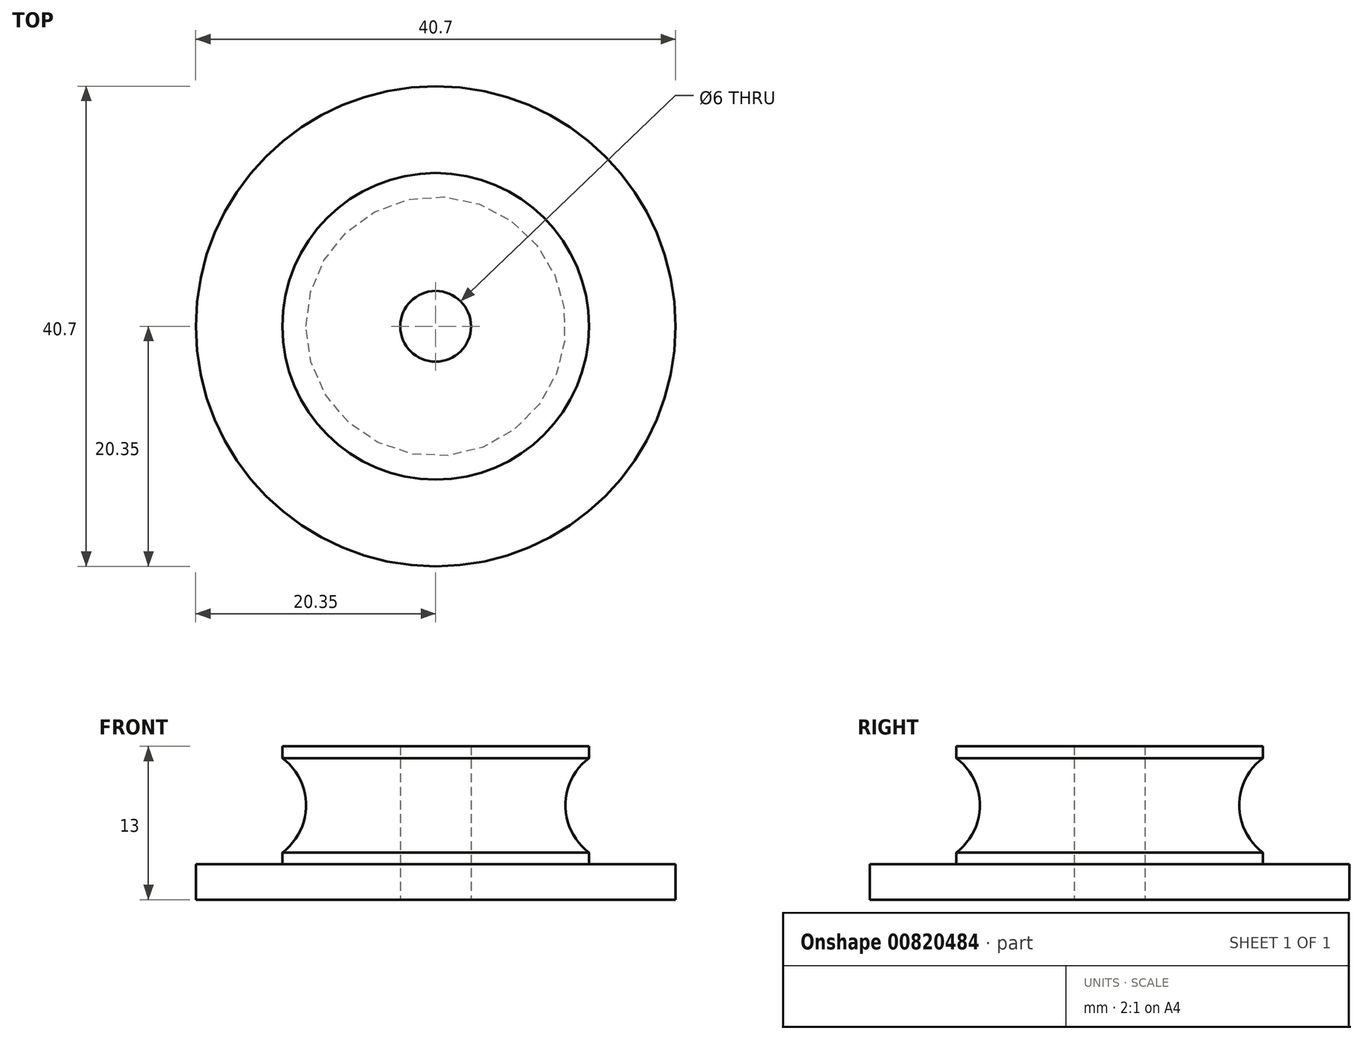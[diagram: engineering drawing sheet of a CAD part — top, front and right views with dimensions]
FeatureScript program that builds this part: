
annotation { "Feature Type Name" : "Feature", "Feature Type Description" : "" }
export const myFeature = defineFeature(function(context is Context, id is Id, definition is map)
    precondition{}
    {
        {
            var Q0;
            Q0=qCreatedBy(makeId("Right.planeOp"),FACE);
            var sketch = newSketch(context, id + "F0", { "sketchPlane" : qUnion([Q0])});
            skLineSegment(sketch, "E0", {"start": v(0, 0) * mm, "end": v(0, 6.45) * mm, "construction": true});
            skLineSegment(sketch, "E1", {"start": v(-3, 0) * mm, "end": v(-3, 5) * mm});
            skLineSegment(sketch, "E2", {"start": v(-3, 5) * mm, "end": v(-13, 5) * mm});
            skLineSegment(sketch, "E3", {"start": v(-13, 5) * mm, "end": v(-13, 4) * mm});
            skLineSegment(sketch, "E4", {"start": v(0, 0) * mm, "end": v(-17.1, 0) * mm, "construction": true});
            skLineSegment(sketch, "E5.MirrorCS", {"start": v(-3, -5) * mm, "end": v(-13, -5) * mm});
            skLineSegment(sketch, "E6.MirrorCS", {"start": v(-3, 0) * mm, "end": v(-3, -5) * mm});
            skLineSegment(sketch, "E7.MirrorCS", {"start": v(-13, -5) * mm, "end": v(-13, -4) * mm});
            skArc(sketch, "E8", {"start": v(-13, -4) * mm, "mid": v(-11, 0) * mm, "end": v(-13, 4) * mm});
            skSolve(sketch);
        }
        {
            var Q0;
            Q0=makeQuery(id+"F0.imprint","IMPRINT",FACE,{"disambiguationData":[TD([[makeQuery(id+"F0.imprint","IMPRINT",EDGE,{"derivedFrom":sQuery(id+"F0.wireOp",EDGE,"E1")}),1.0]])]});
            var Q1;
            Q1=sQuery(id+"F0.wireOp",EDGE,"E0");
            revolve(context, id + "F1", {"surfaceOperationType" : NewSurfaceOperationType.NEW, "entities" : qUnion([Q0]), "axis" : qUnion([Q1]), "revolveType" : RevolveType.FULL});
        }
        {
            var Q0;
            Q0=makeQuery(id+"F1.opRevolve","SWEPT_FACE",FACE,{"disambiguationData":[OSD([sQuery(id+"F0.wireOp",EDGE,"E5.MirrorCS")])]});
            var sketch = newSketch(context, id + "F2", { "sketchPlane" : qUnion([Q0])});
            skCircle(sketch, "E9.0", {"center": v(0, 0) * mm, "radius": 3 * mm});
            skCircle(sketch, "E10", {"center": v(0, 0) * mm, "radius": 20.35 * mm});
            skSolve(sketch);
        }
        {
            var Q0;
            Q0=makeQuery(id+"F2.imprint","IMPRINT",FACE,{"disambiguationData":[TD([[makeQuery(id+"F2.imprint","IMPRINT",EDGE,{"derivedFrom":sQuery(id+"F2.wireOp",EDGE,"E10")}),1.0]])]});
            var Q1;
            Q1=makeQuery(id+"F2.imprint","IMPRINT",FACE,{"disambiguationData":[TD([[makeQuery(id+"F2.imprint","IMPRINT",EDGE,{"derivedFrom":sQuery(id+"F2.wireOp",EDGE,"E9.0")}),-1.0]])]});
            extrude(context, id + "F3", {"entities" : qUnion([Q0, Q1]), "operationType" : NewBodyOperationType.ADD, "depth" : 3 * mm, "offsetDistance" : 25 * mm});
        }
    });
